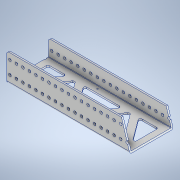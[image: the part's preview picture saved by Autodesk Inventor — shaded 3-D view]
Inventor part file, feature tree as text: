
AUTODESK INVENTOR PART (.ipt)
format: ipt  version: 2020 (Build 240168000, 168)  size: 322,560 bytes
history: native  units: in
note: dims shown in document units (in); Inventor stores cm internally (conversion verified against a paired STEP export)
features: other x3, sketch x2, extrude x1, fillet x1
ambient origin geometry x8: Origin, YZ Plane, XZ Plane, XY Plane, X Axis, Y Axis, Z Axis, Center Point
bodies: Solid1 (feature_tree)
feature tree (7):
  other  "AM14U3 End Sheet PowerCell.ipt"
  extrude  "Extrusion1"  Depth=0.5in
  fillet  "Fillet1"  Radius=0.5in
  other  "Solid1::AM14U3 End Sheet PowerCell.ipt"
  other  "TaggingFeature1"
  sketch  "Sketch1"  dims[d0=0.3937in d1=0.5in d2=0.5in]
  sketch  "Sketch2"  dims[d3=0.5in d4=0.5in d5=0.5in d6=0.5in d8=0.5in d9=0.5in d10=0.0in d11=0.0in d12=0.125in]
